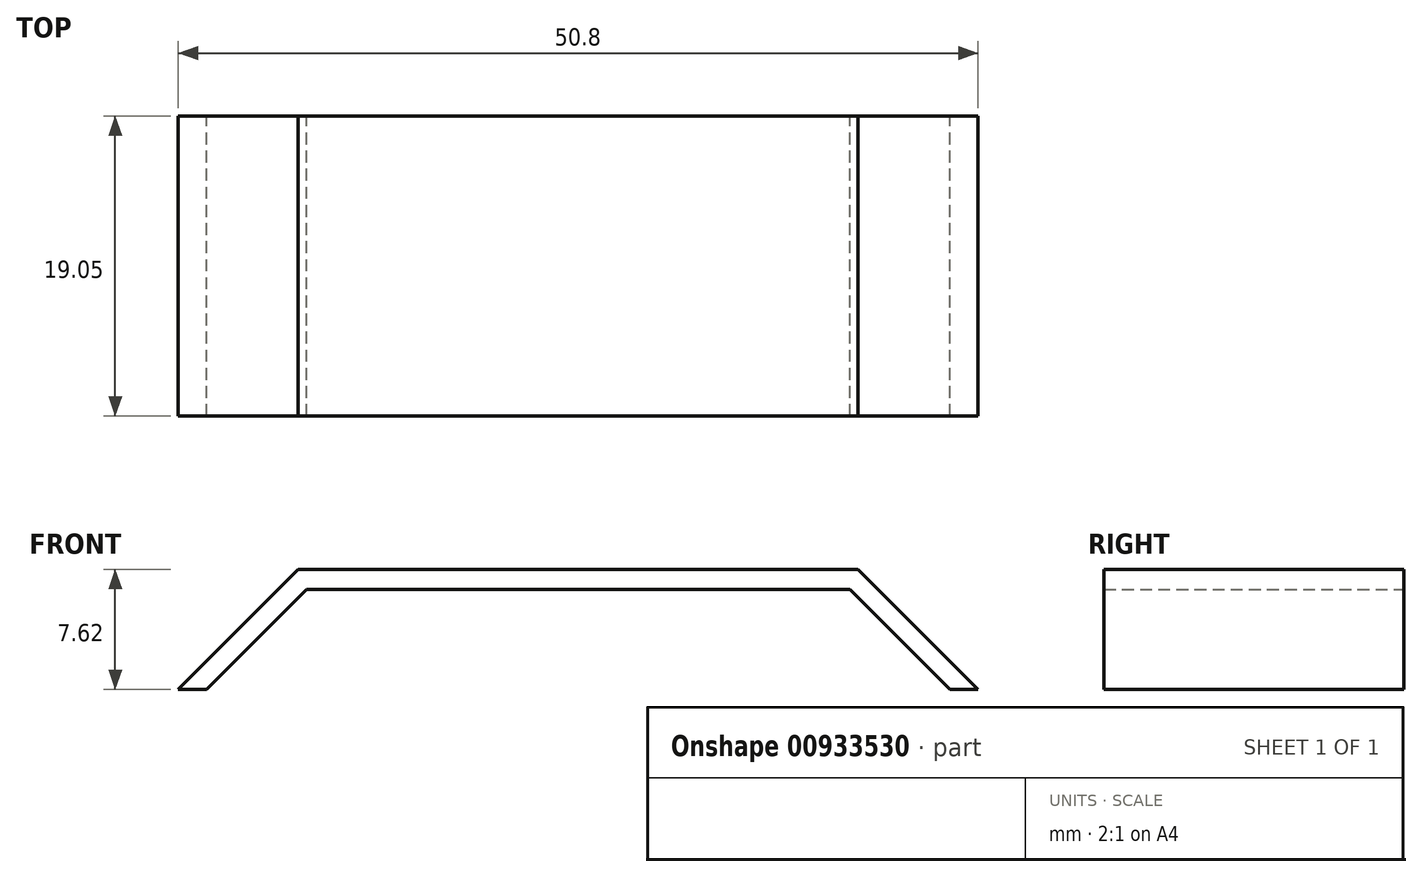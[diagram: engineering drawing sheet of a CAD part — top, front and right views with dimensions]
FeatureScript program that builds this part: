
annotation { "Feature Type Name" : "Feature", "Feature Type Description" : "" }
export const myFeature = defineFeature(function(context is Context, id is Id, definition is map)
    precondition{}
    {
        {
            var Q0;
            Q0=qCreatedBy(makeId("Front.planeOp"),FACE);
            var sketch = newSketch(context, id + "F0", { "sketchPlane" : qUnion([Q0])});
            skLineSegment(sketch, "E0", {"start": v(-46.93, -15.74) * mm, "end": v(-12.42, -15.74) * mm});
            skLineSegment(sketch, "E1", {"start": v(-46.93, -15.74) * mm, "end": v(-53.28, -22.09) * mm});
            skLineSegment(sketch, "E2", {"start": v(-11.9, -14.47) * mm, "end": v(-4.27, -22.09) * mm});
            skLineSegment(sketch, "E3", {"start": v(-53.28, -22.09) * mm, "end": v(-55.07, -22.09) * mm});
            skLineSegment(sketch, "E4", {"start": v(-55.07, -22.09) * mm, "end": v(-47.45, -14.47) * mm});
            skPoint(sketch, "E5.orphan", {"position": v(-0.66, -14.15) * mm});
            skLineSegment(sketch, "E6", {"start": v(-6.07, -22.09) * mm, "end": v(-4.27, -22.09) * mm});
            skLineSegment(sketch, "E7", {"start": v(-47.45, -14.47) * mm, "end": v(-11.9, -14.47) * mm});
            skLineSegment(sketch, "E8", {"start": v(-12.42, -15.74) * mm, "end": v(-6.07, -22.09) * mm});
            skSolve(sketch);
        }
        {
            var Q0;
            Q0=makeQuery(id+"F0.imprint","IMPRINT",FACE,{"disambiguationData":[TD([[makeQuery(id+"F0.imprint","IMPRINT",EDGE,{"derivedFrom":sQuery(id+"F0.wireOp",EDGE,"E0")}),1.0]])]});
            extrude(context, id + "F1", {"entities" : qUnion([Q0]), "flatOperationType" : FlatOperationType.REMOVE, "depth" : 19.05 * mm, "offsetDistance" : 25.4 * mm, "domain" : OperationDomain.MODEL});
        }
    });
